# Revit family: QF_MACOM_CH72C-2M
name_source: partatom
category: Equipamento especial
units: mm (PartAtom-declared; Revit-internal decimal feet)

## family parameters
Com base no plano de trabalho = Não
Compartilhado = Não
Corte com vazios quando carregada = Não
Cota do conector redondo = Utilizar diâmetro
Número OmniClass = 23.40.40.14.17.14
Ponto de cálculo do ambiente = Não
Sempre na vertical = Sim
Tipo de parte = Normal
Título OmniClass = Hot Plates

## types (1)
- CH72C-2M
    Cycle = 60 Hz
    Depth = 745,000 mm
    Descrição = CHAPA 700HP MACOM 720 ELETRICO
    Elec Connection Height = 64,000 mm
    Electric Power = 8000 W
    Elevação padrão = 0,000 mm
    Fabricante = MACOM
    Height = 337,000 mm
    Ingress Protection Code = IP 23
    Modelo = CH72C-2M
    Operational Current = 36 A
    URL = https://www.acosmacom.com.br
    Volts = 220 V
    Volume = 0,18 m³
    Weigth = 110,00 kg
    Width = 720,000 mm

## geometry (parser evidence)
native form markers: Sweep x3
no freeform markers — native parametric forms only
